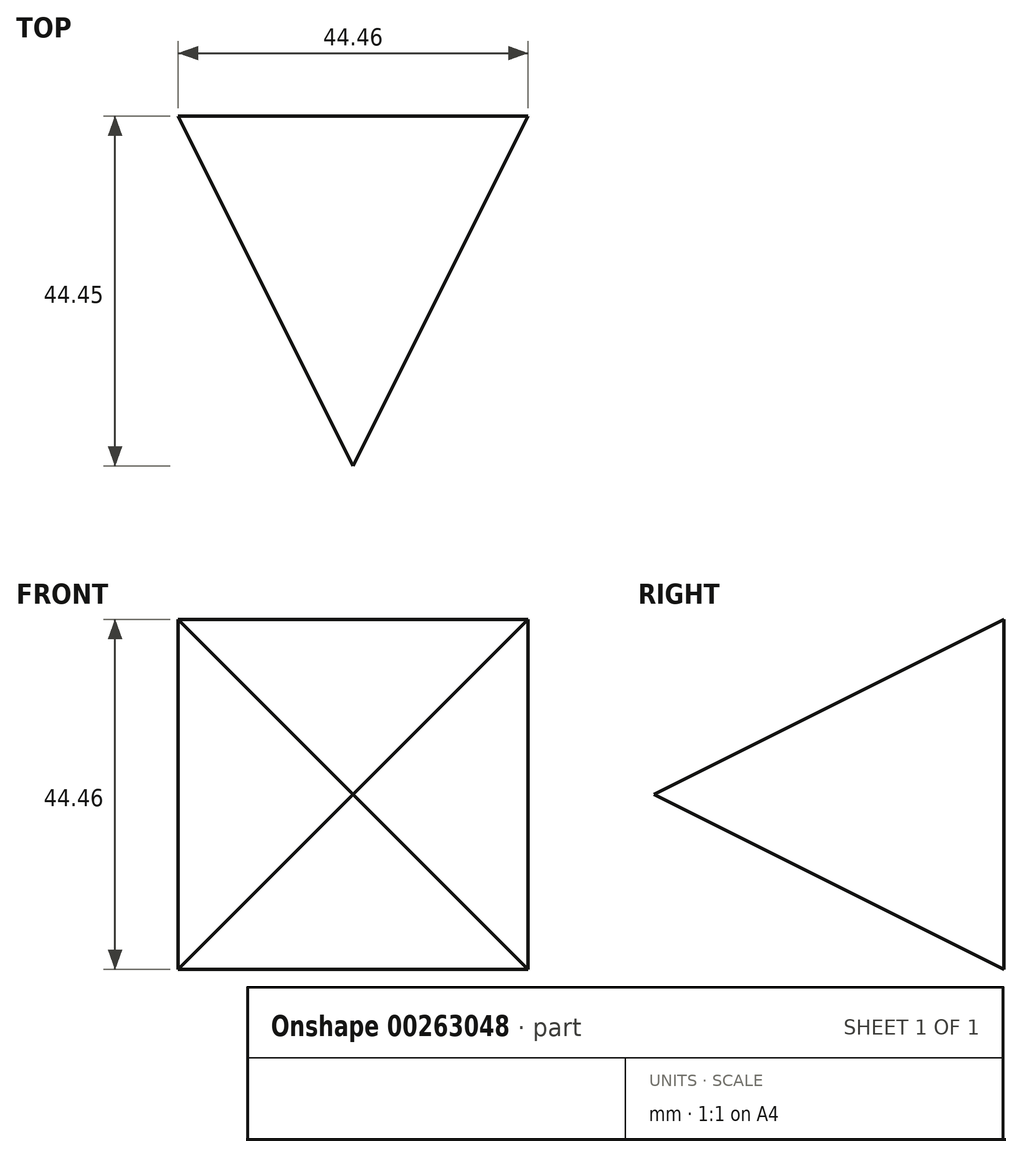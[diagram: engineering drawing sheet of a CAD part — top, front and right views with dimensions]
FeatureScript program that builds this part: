
annotation { "Feature Type Name" : "Feature", "Feature Type Description" : "" }
export const myFeature = defineFeature(function(context is Context, id is Id, definition is map)
    precondition{}
    {
        {
            var Q0;
            Q0=qCreatedBy(makeId("Front.planeOp"),FACE);
            var sketch = newSketch(context, id + "F0", { "sketchPlane" : qUnion([Q0])});
            skLineSegment(sketch, "E0.bottom", {"start": v(22.22, 22.23) * mm, "end": v(-22.23, 22.23) * mm});
            skLineSegment(sketch, "E0.top", {"start": v(22.23, -22.23) * mm, "end": v(-22.22, -22.23) * mm});
            skLineSegment(sketch, "E0.left", {"start": v(22.22, 22.23) * mm, "end": v(22.23, -22.23) * mm});
            skLineSegment(sketch, "E0.right", {"start": v(-22.23, 22.23) * mm, "end": v(-22.22, -22.23) * mm});
            skPoint(sketch, "E0.middle", {"position": v(0, 0) * mm});
            skSolve(sketch);
        }
        {
            var Q0;
            Q0=makeQuery(id+"F0.imprint","IMPRINT",FACE,{"disambiguationData":[TD([[makeQuery(id+"F0.imprint","IMPRINT",EDGE,{"derivedFrom":sQuery(id+"F0.wireOp",EDGE,"E0.bottom")}),1.0]])]});
            extrude(context, id + "F1", {"entities" : qUnion([Q0]), "depth" : 44.45 * mm});
        }
        {
            var Q0;
            Q0=makeQuery(id+"F1.opExtrude","SWEPT_FACE",FACE,{"disambiguationData":[OSD([sQuery(id+"F0.wireOp",EDGE,"E0.right")])]});
            var sketch = newSketch(context, id + "F2", { "sketchPlane" : qUnion([Q0])});
            skLineSegment(sketch, "E1", {"start": v(0, 22.23) * mm, "end": v(44.45, 0) * mm});
            skLineSegment(sketch, "E2", {"start": v(44.45, 0) * mm, "end": v(0, -22.22) * mm});
            skSolve(sketch);
        }
        {
            var Q0;
            Q0=makeQuery(id+"F1.opExtrude","SWEPT_FACE",FACE,{"disambiguationData":[OSD([sQuery(id+"F0.wireOp",EDGE,"E0.top")])]});
            var sketch = newSketch(context, id + "F3", { "sketchPlane" : qUnion([Q0])});
            skLineSegment(sketch, "E3", {"start": v(-22.22, 0) * mm, "end": v(0, 44.45) * mm});
            skLineSegment(sketch, "E4", {"start": v(0, 44.45) * mm, "end": v(22.23, 0) * mm});
            skSolve(sketch);
        }
        {
            var Q0;
            {var subQ0=sQuery(id+"F2.wireOp",EDGE,"E1");Q0=makeQuery(id+"F2.imprint","IMPRINT",FACE,{"disambiguationData":[TD([[makeQuery(id+"F2.imprint","IMPRINT",EDGE,{"derivedFrom":subQ0}),1.0]])]});}
            var Q1;
            {var subQ0=sQuery(id+"F2.wireOp",EDGE,"E2");Q1=makeQuery(id+"F2.imprint","IMPRINT",FACE,{"disambiguationData":[TD([[makeQuery(id+"F2.imprint","IMPRINT",EDGE,{"derivedFrom":subQ0}),1.0]])]});}
            extrude(context, id + "F4", {"entities" : qUnion([Q0, Q1]), "operationType" : NewBodyOperationType.REMOVE, "endBound" : BoundingType.THROUGH_ALL, "oppositeDirection" : true, "depth" : 25.4 * mm});
        }
        {
            var Q0;
            {var subQ0=sQuery(id+"F3.wireOp",EDGE,"E4");Q0=makeQuery(id+"F3.imprint","IMPRINT",FACE,{"disambiguationData":[TD([[makeQuery(id+"F3.imprint","IMPRINT",EDGE,{"derivedFrom":subQ0}),1.0]])]});}
            var Q1;
            {var subQ0=sQuery(id+"F3.wireOp",EDGE,"E3");Q1=makeQuery(id+"F3.imprint","IMPRINT",FACE,{"disambiguationData":[TD([[makeQuery(id+"F3.imprint","IMPRINT",EDGE,{"derivedFrom":subQ0}),1.0]])]});}
            extrude(context, id + "F5", {"entities" : qUnion([Q0, Q1]), "operationType" : NewBodyOperationType.REMOVE, "endBound" : BoundingType.THROUGH_ALL, "oppositeDirection" : true, "depth" : 25.4 * mm});
        }
    });
